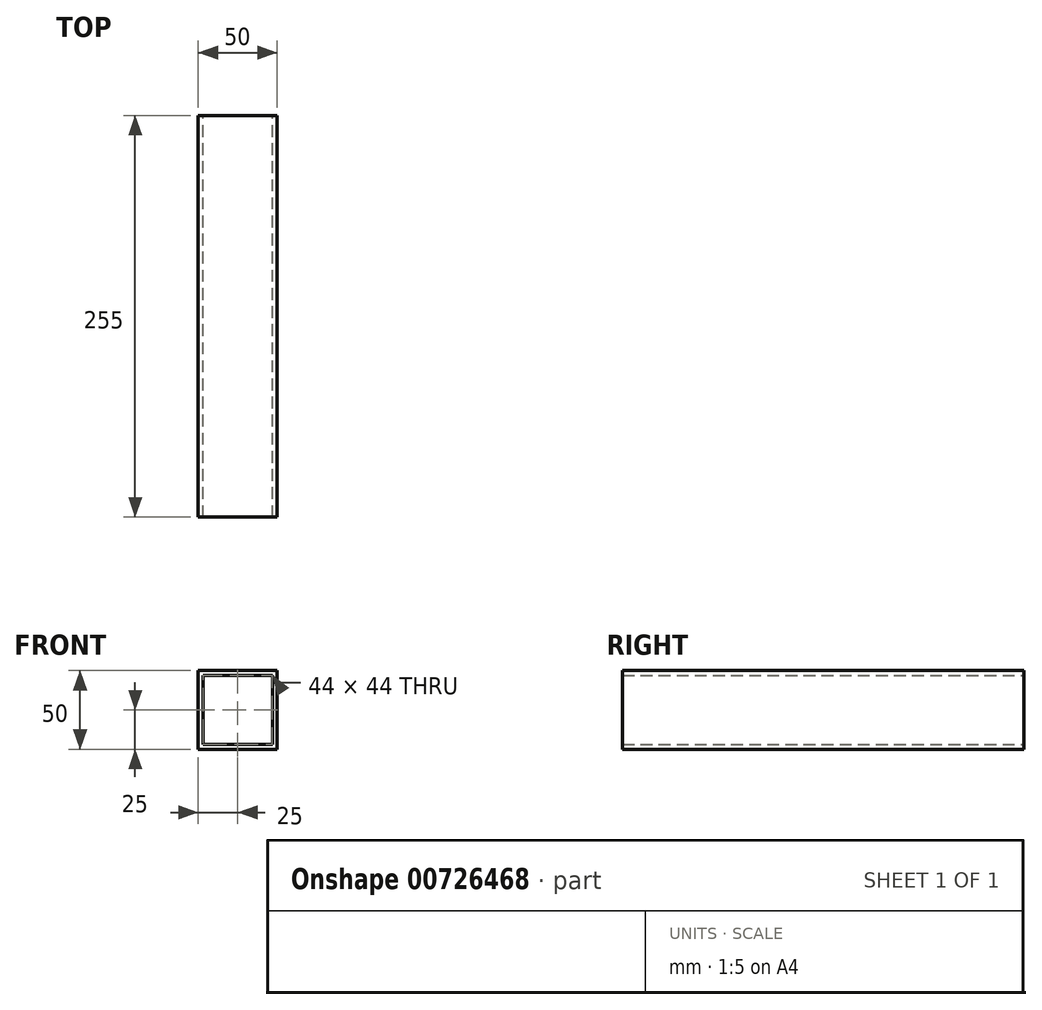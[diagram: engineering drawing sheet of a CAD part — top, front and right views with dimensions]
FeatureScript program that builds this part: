
annotation { "Feature Type Name" : "Feature", "Feature Type Description" : "" }
export const myFeature = defineFeature(function(context is Context, id is Id, definition is map)
    precondition{}
    {
        {
            var Q0;
            Q0=qCreatedBy(makeId("Front.planeOp"),FACE);
            var sketch = newSketch(context, id + "F0", { "sketchPlane" : qUnion([Q0])});
            skLineSegment(sketch, "E0.bottom", {"start": v(0, 0) * mm, "end": v(50, 0) * mm});
            skLineSegment(sketch, "E0.top", {"start": v(0, 50) * mm, "end": v(50, 50) * mm});
            skLineSegment(sketch, "E0.left", {"start": v(0, 0) * mm, "end": v(0, 50) * mm});
            skLineSegment(sketch, "E0.right", {"start": v(50, 0) * mm, "end": v(50, 50) * mm});
            skLineSegment(sketch, "E1.bottom", {"start": v(3, 3) * mm, "end": v(47, 3) * mm});
            skLineSegment(sketch, "E1.top", {"start": v(3, 47) * mm, "end": v(47, 47) * mm});
            skLineSegment(sketch, "E1.left", {"start": v(3, 3) * mm, "end": v(3, 47) * mm});
            skLineSegment(sketch, "E1.right", {"start": v(47, 3) * mm, "end": v(47, 47) * mm});
            skSolve(sketch);
        }
        {
            var Q0;
            Q0=makeQuery(id+"F0.imprint","IMPRINT",FACE,{"disambiguationData":[TD([[makeQuery(id+"F0.imprint","IMPRINT",EDGE,{"derivedFrom":sQuery(id+"F0.wireOp",EDGE,"E0.bottom")}),1.0]])]});
            extrude(context, id + "F1", {"entities" : qUnion([Q0]), "depth" : 255 * mm, "offsetDistance" : 25 * mm});
        }
    });
